# Revit family: Lighting-CommercialSector-GEWISS-ELIA-EL-LED_LUMINAIRES_WALLMOUNTED
name_source: partatom
category: Apparecchi per illuminazione
units: mm (PartAtom-declared; Revit-internal decimal feet)

## family parameters
Condiviso = No
Host = Superficie
Punto di calcolo locali = Sì
Quota connettore circolare = Usa diametro
Sorgente d'illuminazione = Sì
Taglio con vuoti quando caricato = No
Tipo di parte = Normale

## types (12) — shared parameters
Angolo inclinazione = 90.00°
Body = Die-cast aluminium -
Catalogue = LIGHTING
Classification: = -
Color Rendering Index = CRI>80
Colour : = -
Context = Wall / ceiling lighting
DIN 18032-3 certification = -
Device with reduced surface temperature = -
Driver = Included
Driver Box = Built-in
Driver failure rate = F025 = 50.000h Tq 25°C
Electrocod = 2419
Eletrical and lighting features = -
Emetti da diametro cerchio = 220 mm  [stored 0.721785 ft]
External screw = -
File diagramma fotometrico = generic
Filtro dei colori = 16777215
Fixing = Stainless steel support
Gasket = -
General information = -
Glow Wire Test : = 750 °C
IDF = 29759728-ff56-4e85-a590-86c768caeca6
IDT = f04db626-c8ae-45e8-9758-cb7993f1b724
IP degree = IP65
IPEA = -
Immagine tipo = EliaEL.jpg
Installationa and maintenance = -
Insulation class = I
LED Maintenance = Not available
Lifetime = L80B50 (Tq25°C) = 50.000h
Locking Hook = -
Lugnezza massima = 74 mm  [stored 0.242782 ft]
Luminaire = LED luminaire for diffuse light
Materials = -
Maximum surface exposed to the wind : = -
Mouting and installation = Wall and ceiling
Operating temperature : = -20°C - +50°C
Optic = Wide opal
Optic : = -
Optic Maintenance = Not available
Optic and illuminating features = -
Overvoltage protection = DM 0,5KV / CM 1KV
POSIZIONE = 80000
Photobiological Risk Class = RG0
Produttore = GEWISS S.p.A.
Prospetto di default = 1219 mm
Rated frequency (Hz) = 50/60 Hz
Rendi la forma visibile nel rendering = No
SEO = Luminaire
Shield type = Polycarbonate
Shock resistance = IK08
Standard Deviation Colour Matching = SDCM = 5
Standard- = -
Standards and approvals = -
Stocking temperature = -20° +65°
Technical sheet = https://www.gewiss.com
Tilt- = -
Type of light source = LED - Not replaceable
URL = https://www.gewiss.com
Unified Glare Rating = UGR < 25
Unique digital code (Datamatrix) = Currently not present
Variazione temperatura colore lampada con luminosità attenuata = <Nessuno>
Version file RFA = 21.4
Wiring = With connection terminal
larghezza lampada = 50 mm  [stored 0.164042 ft]

## per-type parameters (varying)
| type | Application | Colour | Control System | Descrizione | EAN code | Lumen output (lm) : | Modello | System power : | Versions | Warranty |
| GWF2204LA840 - ELIA EL EMERGENCY 4000K BLACK | Indoor / Outdoor | Black | Emergency | ELIA EL EMERGENCY 4000K BLACK | 8034035077432 | 1650 (440 Em.) | GWF2204LA840 | 18 W | Black Emergency | 3 years |
| GWF2214LA857 - ELIA EL EMERGENCY 5700K WHITE | Indoor / Outdoor | White | Emergency | ELIA EL EMERGENCY 5700K WHITE | 8034035077500 | 1700 (440 Em.) | GWF2214LA857 | 18 W | White Emergency | 3 years |
| GWF2210LA830 - ELIA EL ST AL ON/OFF 3000K WHITE | Indoor / Outdoor | White | Stand alone | ELIA EL ST AL ON/OFF 3000K WHITE | 8034035077517 |  | GWF2210LA830 |  | Standard White | 5 years |
| GWF2200LA857 - ELIA EL ST AL ON/OFF 5700K BLACK | Indoor / Outdoor | Black | Stand alone | ELIA EL ST AL ON/OFF 5700K BLACK | 8034035077470 |  | GWF2200LA857 |  | Standard Black | 5 years |
| GWF2214LA830 - ELIA EL EMERGENCY 3000K WHITE | Indoor / Outdoor | White | Emergency | ELIA EL EMERGENCY 3000K WHITE | 8034035077487 | 1500 (440 Em.) | GWF2214LA830 | 18 W | White Emergency | 3 years |
| GWF2214LA840 - ELIA EL EMERGENCY 4000K WHITE | Indoor / Outdoor | White | Emergency | ELIA EL EMERGENCY 4000K WHITE | 8034035077494 | 1650 (440 Em.) | GWF2214LA840 | 18 W | White Emergency | 3 years |
| GWF2200LA840 - ELIA EL ST AL ON/OFF 4000K BLACK | Indoor / Outdoor | Black | Stand alone | ELIA EL ST AL ON/OFF 4000K BLACK | 8034035077463 |  | GWF2200LA840 |  | Standard Black | 5 years |
| GWF2200LA830 - ELIA EL ST AL ON/OFF 3000K BLACK | External | Black | Stand alone | ELIA EL ST AL ON/OFF 3000K BLACK | 8034035077456 |  | GWF2200LA830 |  | Standard Black | 5 years |
| GWF2210LA840 - ELIA EL ST AL ON/OFF 4000K WHITE | Indoor / Outdoor | White | Stand alone | ELIA EL ST AL ON/OFF 4000K WHITE | 8034035077524 |  | GWF2210LA840 |  | Standard White | 5 years |
| GWF2204LA857 - ELIA EL EMERGENCY 5700K BLACK | Indoor / Outdoor | Black | Emergency | ELIA EL EMERGENCY 5700K BLACK | 8034035077449 | 1700 (440 Em.) | GWF2204LA857 | 18 W | Black Emergency | 3 years |
| GWF2204LA830 - ELIA EL EMERGENCY 3000K BLACK | Indoor / Outdoor | Black | Emergency | ELIA EL EMERGENCY 3000K BLACK | 8034035077425 | 1500 (440 Em.) | GWF2204LA830 | 18 W | Black Emergency | 3 years |
| GWF2210LA857 - ELIA EL ST AL ON/OFF 5700K WHITE | Indoor / Outdoor | White | Stand alone | ELIA EL ST AL ON/OFF 5700K WHITE | 8034035077531 |  | GWF2210LA857 |  | Standard White | 5 years |

note: [stored X ft] marks values corroborated as IEEE doubles in the binary element streams (Revit-internal decimal feet)
